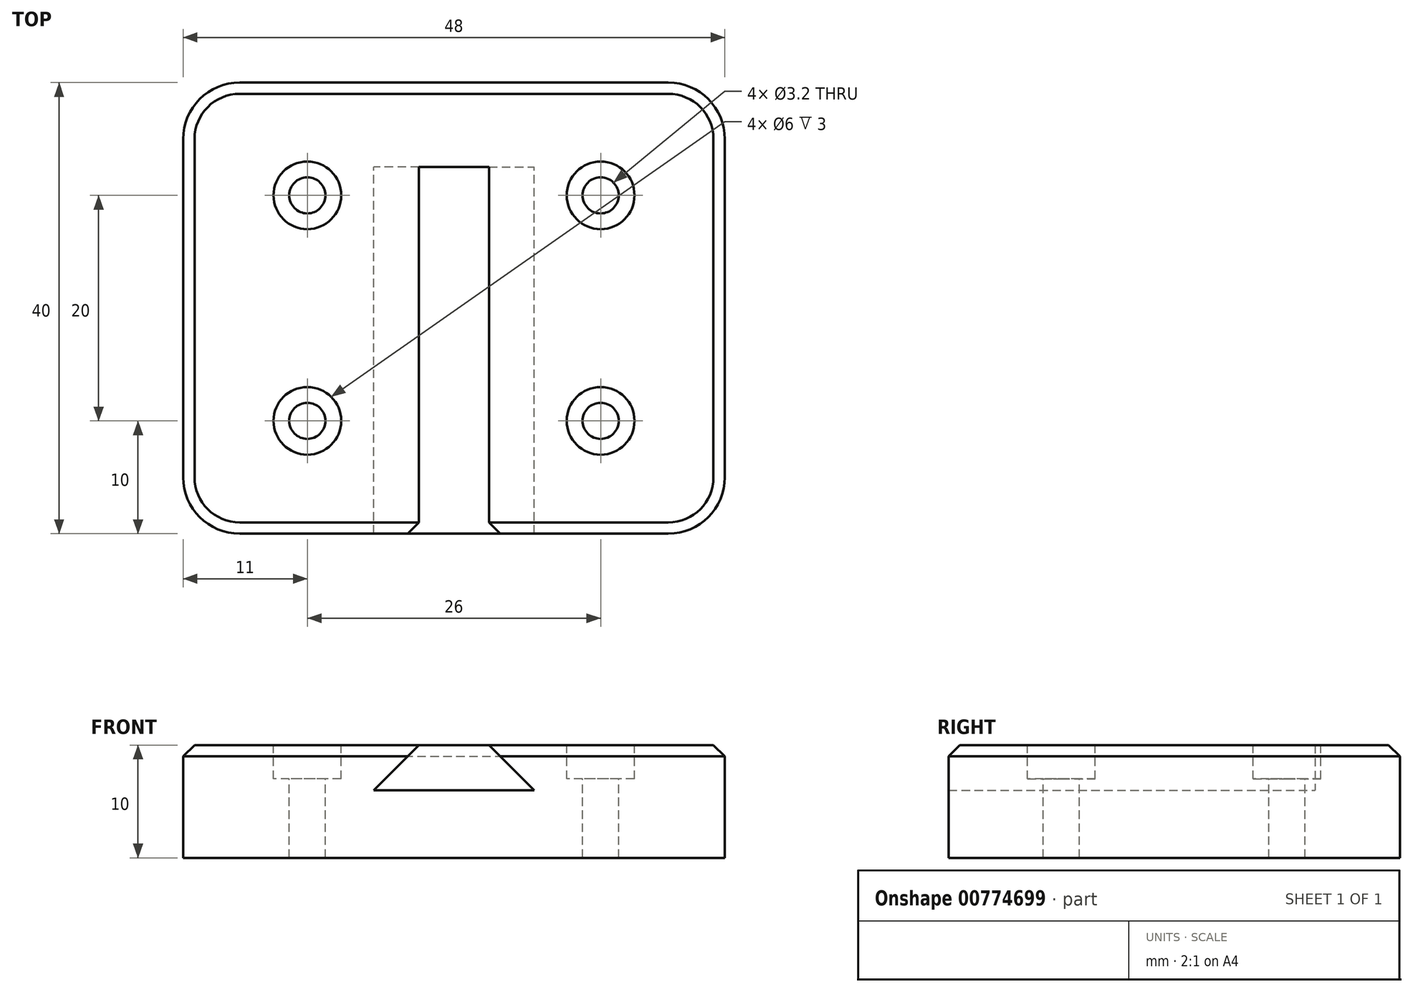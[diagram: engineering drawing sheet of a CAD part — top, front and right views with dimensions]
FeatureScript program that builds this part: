
annotation { "Feature Type Name" : "Feature", "Feature Type Description" : "" }
export const myFeature = defineFeature(function(context is Context, id is Id, definition is map)
    precondition{}
    {
        {
            var Q0;
            Q0=qCreatedBy(makeId("Front.planeOp"),FACE);
            var sketch = newSketch(context, id + "F0", { "sketchPlane" : qUnion([Q0])});
            skLineSegment(sketch, "E0", {"start": v(-24, 0) * mm, "end": v(-24, -6) * mm});
            skLineSegment(sketch, "E1", {"start": v(-24, -6) * mm, "end": v(24, -6) * mm});
            skLineSegment(sketch, "E2", {"start": v(24, -6) * mm, "end": v(24, 0) * mm});
            skLineSegment(sketch, "E3", {"start": v(-24, 0) * mm, "end": v(-24, 4) * mm});
            skLineSegment(sketch, "E4", {"start": v(-24, 4) * mm, "end": v(-3.1, 4) * mm});
            skLineSegment(sketch, "E5", {"start": v(-3.1, 4) * mm, "end": v(-7.1, 0) * mm});
            skLineSegment(sketch, "E6", {"start": v(-7.1, 0) * mm, "end": v(7.1, 0) * mm});
            skLineSegment(sketch, "E7", {"start": v(7.1, 0) * mm, "end": v(3.1, 4) * mm});
            skLineSegment(sketch, "E8", {"start": v(3.1, 4) * mm, "end": v(24, 4) * mm});
            skLineSegment(sketch, "E9", {"start": v(24, 4) * mm, "end": v(24, 0) * mm});
            skSolve(sketch);
        }
        {
            var Q0;
            Q0=makeQuery(id+"F0.imprint","IMPRINT",FACE,{"disambiguationData":[TD([[makeQuery(id+"F0.imprint","IMPRINT",EDGE,{"derivedFrom":sQuery(id+"F0.wireOp",EDGE,"E0")}),1.0]])]});
            extrude(context, id + "F1", {"entities" : qUnion([Q0]), "endBound" : BoundingType.SYMMETRIC, "depth" : 40 * mm, "offsetDistance" : 25 * mm});
        }
        {
            var Q0;
            Q0=makeQuery(id+"F1.opExtrude","CAP_EDGE",EDGE,{"disambiguationData":[OSD([sQuery(id+"F0.wireOp",EDGE,"E0"),sQuery(id+"F0.wireOp",EDGE,"E3")])],"isStart":true});
            var Q1;
            Q1=makeQuery(id+"F1.opExtrude","CAP_EDGE",EDGE,{"disambiguationData":[OSD([sQuery(id+"F0.wireOp",EDGE,"E2"),sQuery(id+"F0.wireOp",EDGE,"E9")])],"isStart":true});
            var Q2;
            Q2=makeQuery(id+"F1.opExtrude","CAP_EDGE",EDGE,{"disambiguationData":[OSD([sQuery(id+"F0.wireOp",EDGE,"E2"),sQuery(id+"F0.wireOp",EDGE,"E9")])],"isStart":false});
            var Q3;
            Q3=makeQuery(id+"F1.opExtrude","CAP_EDGE",EDGE,{"disambiguationData":[OSD([sQuery(id+"F0.wireOp",EDGE,"E0"),sQuery(id+"F0.wireOp",EDGE,"E3")])],"isStart":false});
            fillet(context, id + "F2", {"entities" : qUnion([Q0, Q1, Q2, Q3]), "radius" : 5 * mm, "tangentPropagation" : true, "allowEdgeOverflow" : false});
        }
        {
            var Q0;
            Q0=makeQuery(id+"F2.opFillet","BLEND_EDGE",EDGE,{"blendedFrom":[makeQuery(id+"F1.opExtrude","CAP_EDGE",EDGE,{"disambiguationData":[OSD([sQuery(id+"F0.wireOp",EDGE,"E0"),sQuery(id+"F0.wireOp",EDGE,"E3")])],"isStart":false}),makeQuery(id+"F1.opExtrude","SWEPT_FACE",FACE,{"disambiguationData":[OSD([sQuery(id+"F0.wireOp",EDGE,"E4")])]})],"blendedInto":[makeQuery(id+"F1.opExtrude","SWEPT_FACE",FACE,{"disambiguationData":[OSD([sQuery(id+"F0.wireOp",EDGE,"E4")])]})]});
            var Q1;
            Q1=makeQuery(id+"F1.opExtrude","CAP_EDGE",EDGE,{"disambiguationData":[OSD([sQuery(id+"F0.wireOp",EDGE,"E8")])],"isStart":false});
            chamfer(context, id + "F3", {"entities" : qUnion([Q0, Q1]), "width" : 1 * mm, "tangentPropagation" : true});
        }
        {
            var Q0;
            Q0=makeQuery(id+"F1.opExtrude","SWEPT_FACE",FACE,{"disambiguationData":[OSD([sQuery(id+"F0.wireOp",EDGE,"E8")])]});
            var sketch = newSketch(context, id + "F4", { "sketchPlane" : qUnion([Q0])});
            skPoint(sketch, "E10", {"position": v(13, -10) * mm});
            skPoint(sketch, "E11", {"position": v(13, 10) * mm});
            skPoint(sketch, "E12.MirrorP", {"position": v(-13, -10) * mm});
            skPoint(sketch, "E13.MirrorP", {"position": v(-13, 10) * mm});
            skSolve(sketch);
        }
        {
            var Q0;
            Q0=sQuery(id+"F4.wireOp",VERTEX,"E10");
            var Q1;
            Q1=sQuery(id+"F4.wireOp",VERTEX,"E12.MirrorP");
            var Q2;
            Q2=sQuery(id+"F4.wireOp",VERTEX,"E11");
            var Q3;
            Q3=sQuery(id+"F4.wireOp",VERTEX,"E13.MirrorP");
            var Q4;
            Q4=makeQuery(id+"F1.opExtrude","SWEPT_BODY",BODY,{"disambiguationData":[OSD([sQuery(id+"F0.wireOp",EDGE,"E0"),sQuery(id+"F0.wireOp",EDGE,"E1"),sQuery(id+"F0.wireOp",EDGE,"E2"),sQuery(id+"F0.wireOp",EDGE,"E3"),sQuery(id+"F0.wireOp",EDGE,"E4"),sQuery(id+"F0.wireOp",EDGE,"E5"),sQuery(id+"F0.wireOp",EDGE,"E6"),sQuery(id+"F0.wireOp",EDGE,"E7"),sQuery(id+"F0.wireOp",EDGE,"E8"),sQuery(id+"F0.wireOp",EDGE,"E9")])]});
            hole(context, id + "F5", {"style" : HoleStyle.C_BORE, "endStyle" : HoleEndStyle.THROUGH, "holeDiameter" : 3.2 * mm, "cBoreDiameter" : 6 * mm, "cBoreDepth" : 3 * mm, "majorDiameter" : 5 * mm, "isTappedThrough" : true, "tappedDepth" : 12 * mm, "tapClearance" : 3, "startFromSketch" : true, "locations" : qUnion([Q0, Q1, Q2, Q3]), "scope" : qUnion([Q4])});
        }
        {
            var Q0;
            Q0=makeQuery(id+"F1.opExtrude","SWEPT_FACE",FACE,{"disambiguationData":[OSD([sQuery(id+"F0.wireOp",EDGE,"E1")])]});
            var sketch = newSketch(context, id + "F6", { "sketchPlane" : qUnion([Q0])});
            skLineSegment(sketch, "E14.bottom", {"start": v(-9, -12.5) * mm, "end": v(9, -12.5) * mm});
            skLineSegment(sketch, "E14.top", {"start": v(-9, -20) * mm, "end": v(9, -20) * mm});
            skLineSegment(sketch, "E14.left", {"start": v(-9, -12.5) * mm, "end": v(-9, -20) * mm});
            skLineSegment(sketch, "E14.right", {"start": v(9, -12.5) * mm, "end": v(9, -20) * mm});
            skSolve(sketch);
        }
        {
            var Q0;
            Q0 = qSketchRegion(id + "F6", true);
            extrude(context, id + "F7", {"entities" : qUnion([Q0]), "operationType" : NewBodyOperationType.ADD, "oppositeDirection" : true, "depth" : 10 * mm, "offsetDistance" : 25 * mm});
        }
        {
            var Q0;
            Q0=makeQuery(id+"F7.opExtrude","CAP_EDGE",EDGE,{"disambiguationData":[OSD([sQuery(id+"F6.wireOp",EDGE,"E14.top")])],"isStart":false});
            chamfer(context, id + "F8", {"entities" : qUnion([Q0]), "width" : 1 * mm, "tangentPropagation" : true});
        }
    });
